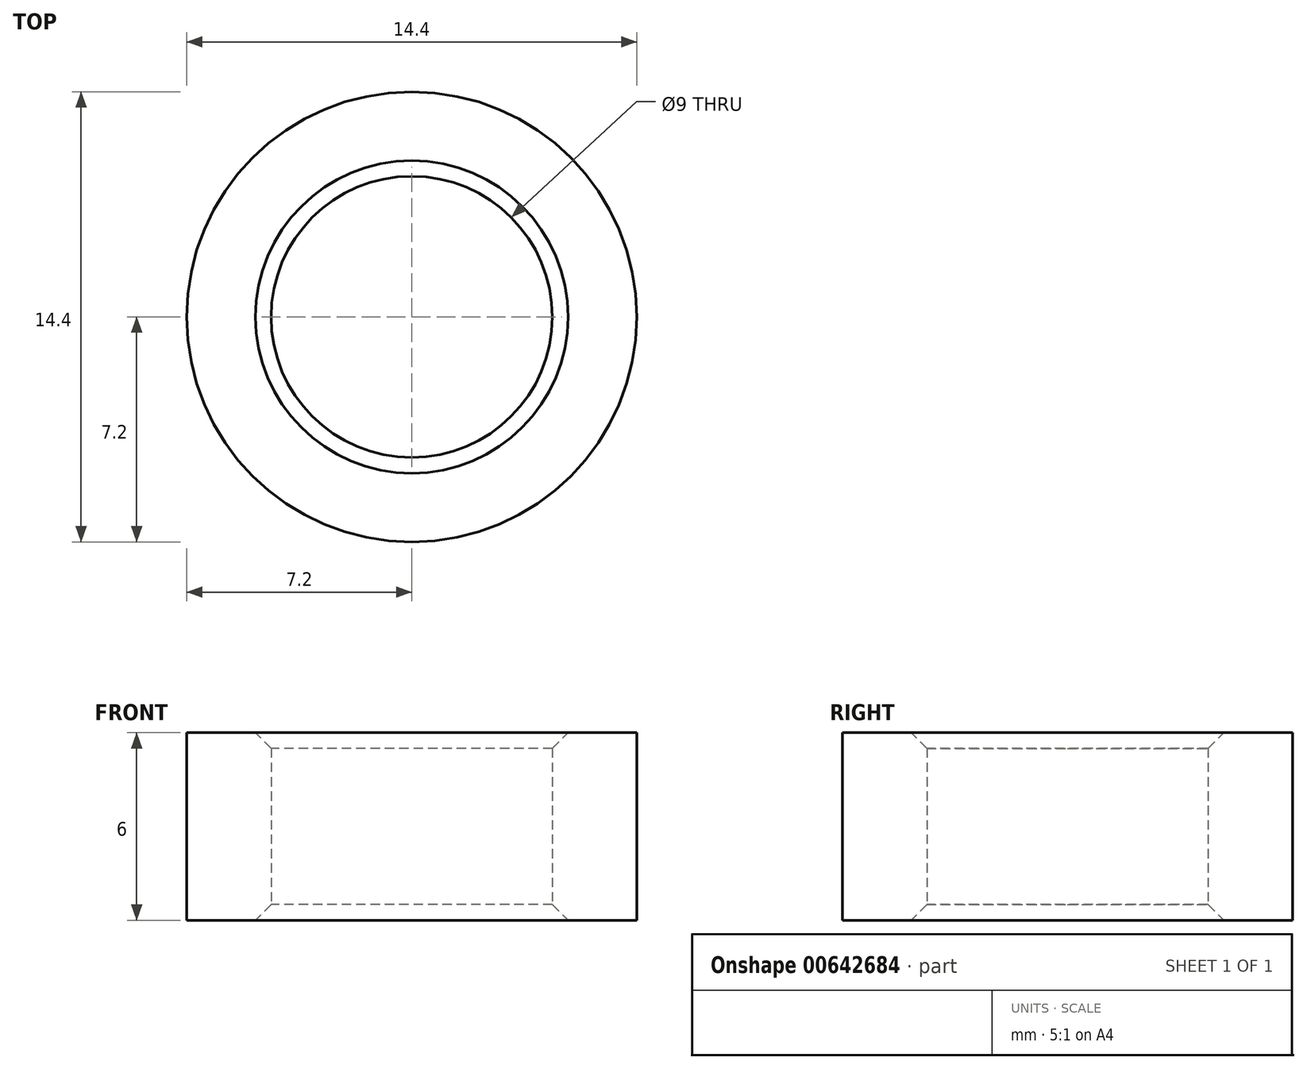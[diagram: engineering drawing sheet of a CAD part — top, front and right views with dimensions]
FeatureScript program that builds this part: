
annotation { "Feature Type Name" : "Feature", "Feature Type Description" : "" }
export const myFeature = defineFeature(function(context is Context, id is Id, definition is map)
    precondition{}
    {
        {
            var Q0;
            Q0=qCreatedBy(makeId("Top.planeOp"),FACE);
            var sketch = newSketch(context, id + "F0", { "sketchPlane" : qUnion([Q0])});
            skCircle(sketch, "E0", {"center": v(0, 0) * mm, "radius": 7.2 * mm});
            skCircle(sketch, "E1", {"center": v(0, 0) * mm, "radius": 4.5 * mm});
            skSolve(sketch);
        }
        {
            var Q0;
            Q0 = qSketchRegion(id + "F0", true);
            extrude(context, id + "F1", {"entities" : qUnion([Q0]), "depth" : 6 * mm, "offsetDistance" : 25.4 * mm});
        }
        {
            var Q0;
            Q0=makeQuery(id+"F1.opExtrude","CAP_EDGE",EDGE,{"disambiguationData":[OSD([sQuery(id+"F0.wireOp",EDGE,"E1")])],"isStart":true});
            var Q1;
            Q1=makeQuery(id+"F1.opExtrude","SWEPT_FACE",FACE,{"disambiguationData":[OSD([sQuery(id+"F0.wireOp",EDGE,"E1")])]});
            chamfer(context, id + "F2", {"entities" : qUnion([Q0, Q1]), "chamferType" : ChamferType.OFFSET_ANGLE, "width" : 0.5 * mm, "oppositeDirection" : false, "angle" : 45 * degree, "tangentPropagation" : true});
        }
    });
